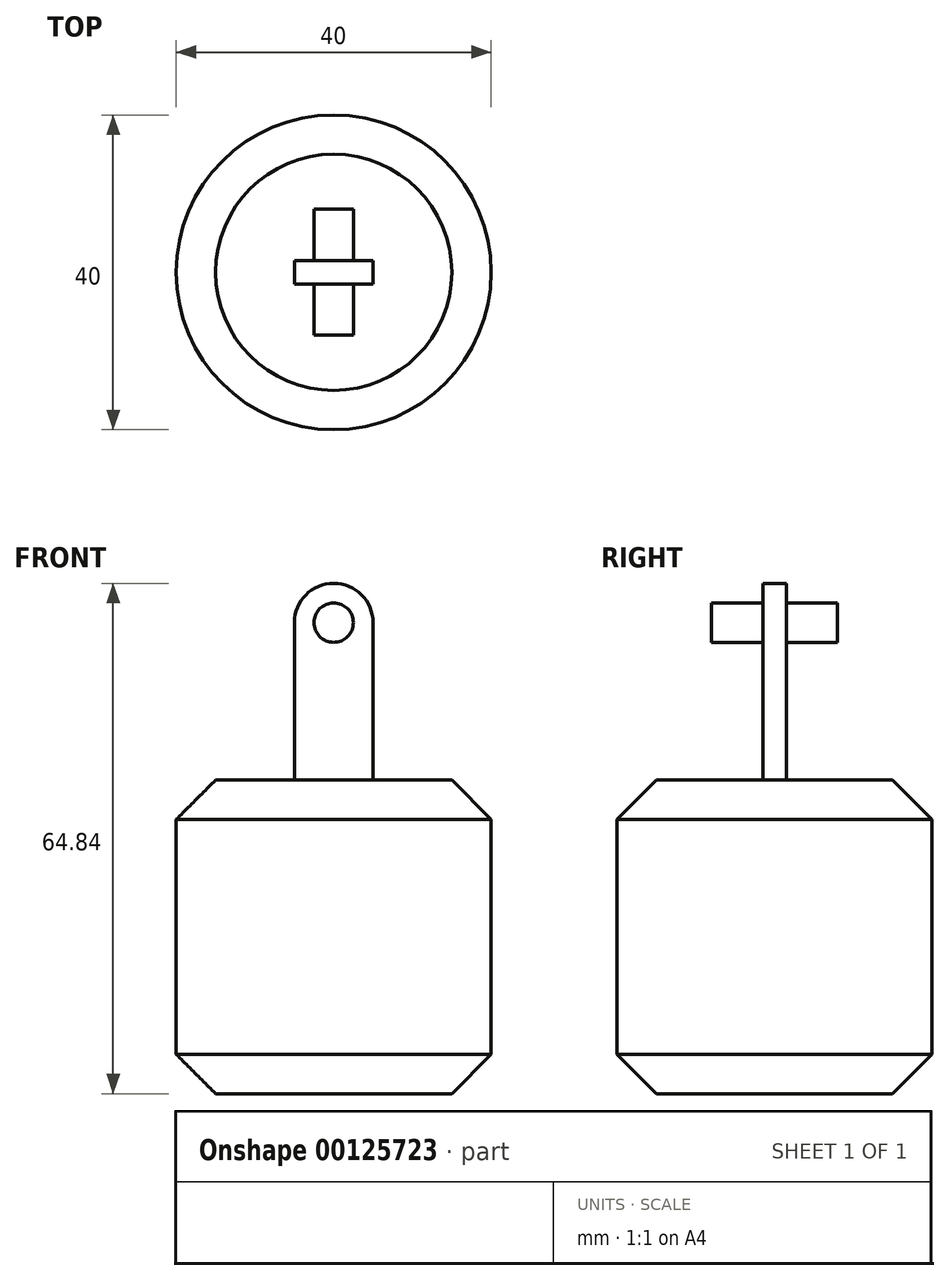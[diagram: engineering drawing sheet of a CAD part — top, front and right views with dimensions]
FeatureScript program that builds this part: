
annotation { "Feature Type Name" : "Feature", "Feature Type Description" : "" }
export const myFeature = defineFeature(function(context is Context, id is Id, definition is map)
    precondition{}
    {
        {
            var Q0;
            Q0=qCreatedBy(makeId("Front.planeOp"),FACE);
            var sketch = newSketch(context, id + "F0", { "sketchPlane" : qUnion([Q0])});
            skCircle(sketch, "E0", {"center": v(0, 0) * mm, "radius": 2.5 * mm});
            skSolve(sketch);
        }
        {
            var Q0;
            Q0 = qSketchRegion(id + "F0", true);
            extrude(context, id + "F1", {"entities" : qUnion([Q0]), "depth" : 16 * mm, "symmetric" : true});
        }
        {
            var Q0;
            Q0=qCreatedBy(makeId("Front.planeOp"),FACE);
            var sketch = newSketch(context, id + "F2", { "sketchPlane" : qUnion([Q0])});
            skArc(sketch, "E1", {"start": v(-5, 0) * mm, "mid": v(0, 5) * mm, "end": v(5, 0) * mm});
            skLineSegment(sketch, "E2", {"start": v(-5, 0) * mm, "end": v(-5, -20) * mm});
            skLineSegment(sketch, "E3", {"start": v(5, 0) * mm, "end": v(5, -20) * mm});
            skLineSegment(sketch, "E4", {"start": v(5, -20) * mm, "end": v(-5, -20) * mm});
            skSolve(sketch);
        }
        {
            var Q0;
            Q0 = qSketchRegion(id + "F2", true);
            extrude(context, id + "F3", {"entities" : qUnion([Q0]), "operationType" : NewBodyOperationType.ADD, "depth" : 3 * mm, "symmetric" : true});
        }
        {
            var Q0;
            Q0=makeQuery(id+"F3.opExtrude","SWEPT_FACE",FACE,{"disambiguationData":[OSD([sQuery(id+"F2.wireOp",EDGE,"E4")])]});
            var sketch = newSketch(context, id + "F4", { "sketchPlane" : qUnion([Q0])});
            skCircle(sketch, "E5", {"center": v(0, 0) * mm, "radius": 20 * mm});
            skSolve(sketch);
        }
        {
            var Q0;
            Q0 = qSketchRegion(id + "F4", true);
            extrude(context, id + "F5", {"entities" : qUnion([Q0]), "operationType" : NewBodyOperationType.ADD, "depth" : 39.84 * mm});
        }
        {
            var Q0;
            Q0=makeQuery(id+"F5.opExtrude","CAP_EDGE",EDGE,{"disambiguationData":[OSD([sQuery(id+"F4.wireOp",EDGE,"E5")])],"isStart":true});
            var Q1;
            Q1=makeQuery(id+"F5.opExtrude","CAP_EDGE",EDGE,{"disambiguationData":[OSD([sQuery(id+"F4.wireOp",EDGE,"E5")])],"isStart":false});
            chamfer(context, id + "F6", {"entities" : qUnion([Q0, Q1]), "width" : 5 * mm, "tangentPropagation" : true});
        }
    });
